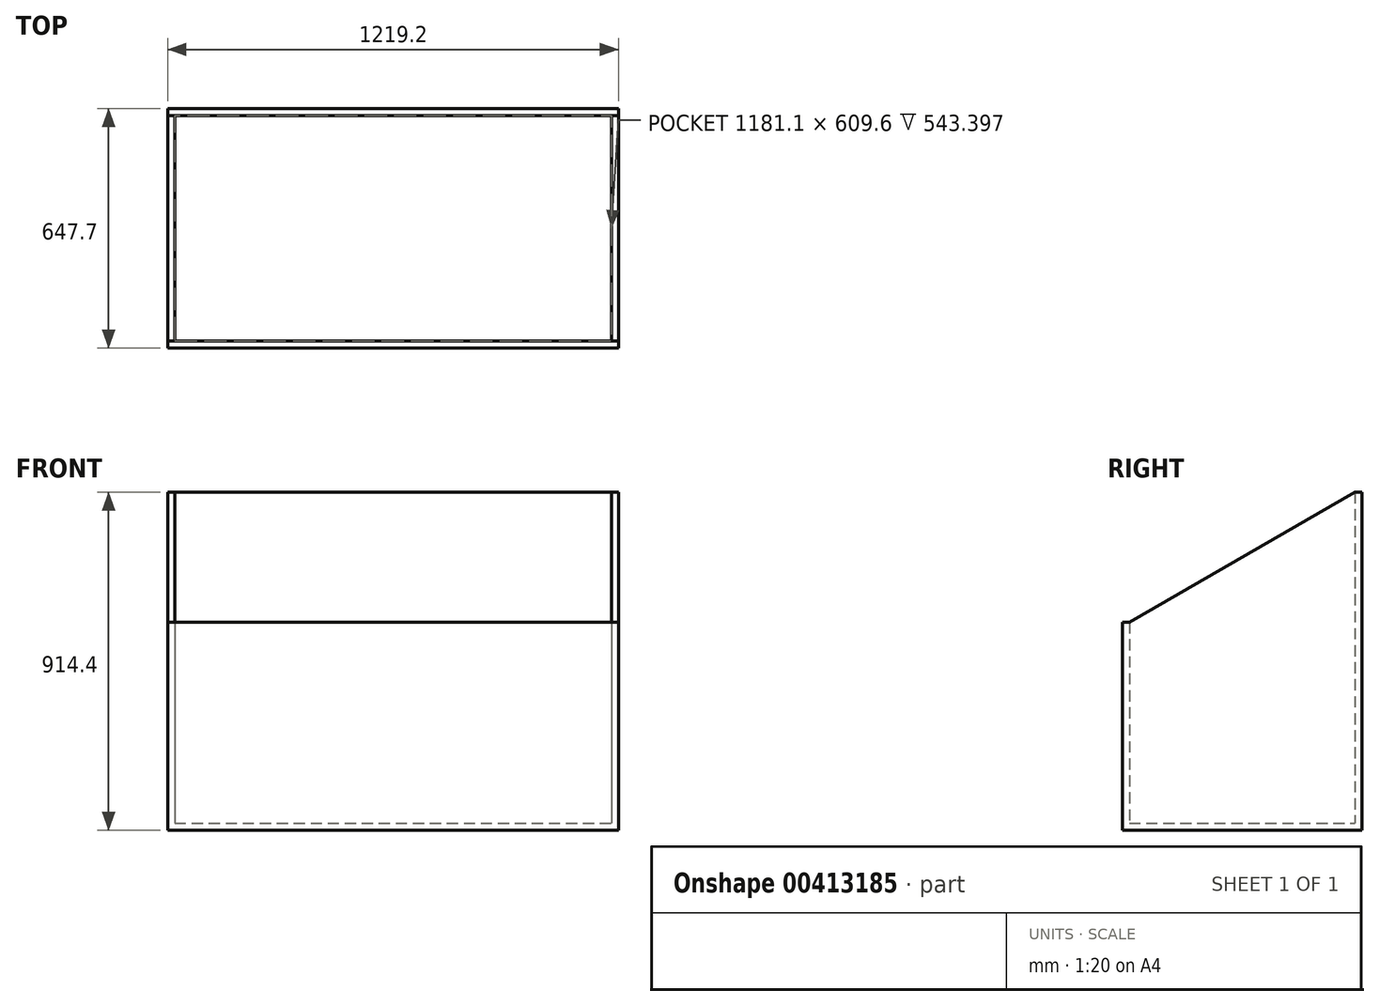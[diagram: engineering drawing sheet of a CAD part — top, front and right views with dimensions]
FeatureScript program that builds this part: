
annotation { "Feature Type Name" : "Feature", "Feature Type Description" : "" }
export const myFeature = defineFeature(function(context is Context, id is Id, definition is map)
    precondition{}
    {
        {
            var Q0;
            Q0=qCreatedBy(makeId("Right.planeOp"),FACE);
            var sketch = newSketch(context, id + "F0", { "sketchPlane" : qUnion([Q0])});
            skLineSegment(sketch, "E0", {"start": v(0, 0) * mm, "end": v(0, 914.4) * mm});
            skLineSegment(sketch, "E1", {"start": v(-19.05, 914.4) * mm, "end": v(-628.65, 562.45) * mm});
            skLineSegment(sketch, "E2", {"start": v(-647.7, 0) * mm, "end": v(0, 0) * mm});
            skLineSegment(sketch, "E3", {"start": v(-19.05, 914.4) * mm, "end": v(0, 914.4) * mm});
            skLineSegment(sketch, "E4", {"start": v(-628.65, 562.45) * mm, "end": v(-647.7, 562.45) * mm});
            skLineSegment(sketch, "E5", {"start": v(-647.7, 562.45) * mm, "end": v(-647.7, 0) * mm});
            skSolve(sketch);
        }
        {
            var Q0;
            Q0=makeQuery(id+"F0.imprint","IMPRINT",FACE,{"disambiguationData":[TD([[makeQuery(id+"F0.imprint","IMPRINT",EDGE,{"derivedFrom":sQuery(id+"F0.wireOp",EDGE,"E0")}),1.0]])]});
            extrude(context, id + "F1", {"entities" : qUnion([Q0]), "endBound" : BoundingType.SYMMETRIC, "oppositeDirection" : true, "depth" : 1219.2 * mm});
        }
        {
            var Q0;
            Q0=qCreatedBy(makeId("Right.planeOp"),FACE);
            var sketch = newSketch(context, id + "F2", { "sketchPlane" : qUnion([Q0])});
            skLineSegment(sketch, "E6.0.1", {"start": v(-628.65, 562.45) * mm, "end": v(-647.7, 562.45) * mm, "construction": true});
            skLineSegment(sketch, "E6.0.2", {"start": v(-647.7, 562.45) * mm, "end": v(-647.7, 0) * mm});
            skLineSegment(sketch, "E6.0.3", {"start": v(-647.7, 0) * mm, "end": v(0, 0) * mm});
            skLineSegment(sketch, "E6.0.4", {"start": v(0, 0) * mm, "end": v(0, 914.4) * mm});
            skLineSegment(sketch, "E7.bottom", {"start": v(-628.65, 1035.05) * mm, "end": v(-19.05, 1035.05) * mm});
            skLineSegment(sketch, "E7.top", {"start": v(-628.65, 19.05) * mm, "end": v(-19.05, 19.05) * mm});
            skLineSegment(sketch, "E7.left", {"start": v(-628.65, 1035.05) * mm, "end": v(-628.65, 19.05) * mm});
            skLineSegment(sketch, "E7.right", {"start": v(-19.05, 1035.05) * mm, "end": v(-19.05, 19.05) * mm});
            skSolve(sketch);
        }
        {
            var Q0;
            Q0=makeQuery(id+"F2.imprint","IMPRINT",FACE,{"disambiguationData":[TD([[makeQuery(id+"F2.imprint","IMPRINT",EDGE,{"derivedFrom":sQuery(id+"F2.wireOp",EDGE,"E7.bottom")}),-1.0]])]});
            extrude(context, id + "F3", {"entities" : qUnion([Q0]), "operationType" : NewBodyOperationType.REMOVE, "endBound" : BoundingType.SYMMETRIC, "oppositeDirection" : true, "depth" : 1181.1 * mm});
        }
    });
